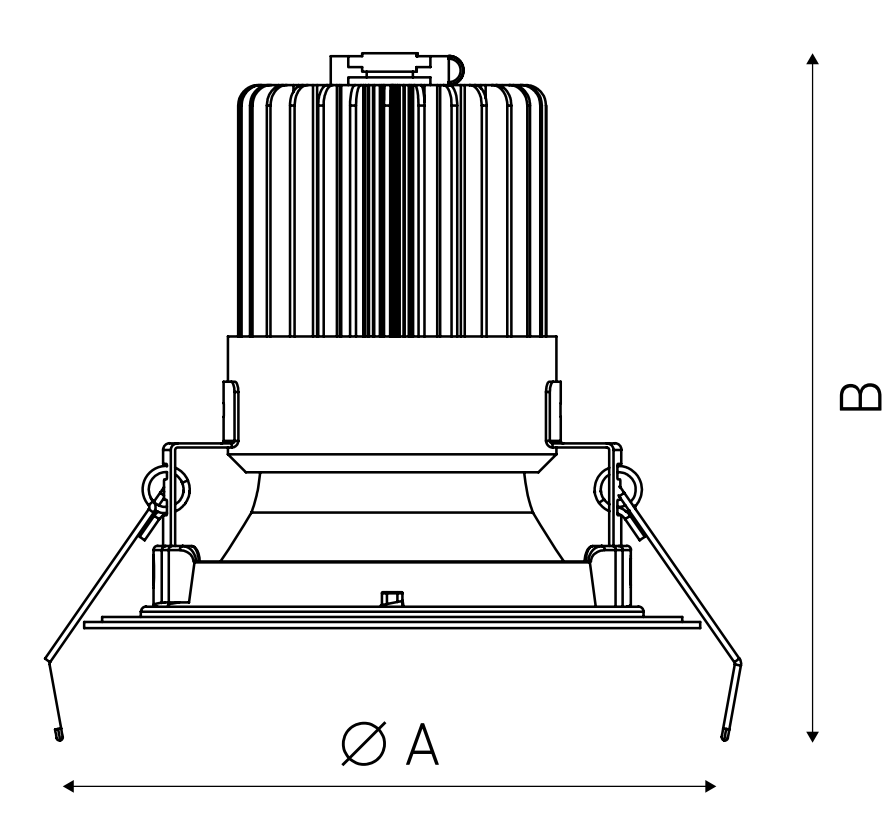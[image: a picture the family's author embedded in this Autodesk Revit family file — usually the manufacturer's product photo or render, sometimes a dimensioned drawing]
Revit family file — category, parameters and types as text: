
# Revit family: OKKO S
name_source: partatom
category: Осветительные приборы
revit_build: Autodesk Revit 2016 (Build: 20150220_1215(x64)
units: mm (PartAtom-declared; Revit-internal decimal feet)

## family parameters
Источник света = Да
Общий = Нет
Основа = Грань
При загрузке вырезать с полостями = Нет
Размер круглого соединителя = Использовать диаметр
Тип детали = Нормальный
Точка расчета площади = Нет

## types (1)
- OKKO S
    ADSK_Единица измерения = Шт.
    ADSK_Завод-изготовитель = ООО МГК Световые технологии
    ADSK_Количество фаз = 1
    ADSK_Количество фаз числовое = 1
    ADSK_Коэффициент мощности = 0.92
    ADSK_Масса = 0
    ADSK_Наименование = Накладной потолочный светодиодный светильник направленного света. Корпус светильника выполнен из алюминия, окрашенного матовой краской. Глубокая декоративная рамка из зеркального алюминия создает большой защитный угол и эффект выключенного источника света – dark light. Оптическая часть закрыта фасетчатым стеклом. Стандартный цвет WH – белый
    ADSK_Напряжение = 220 В
    ADSK_Номинальная мощность = 0 кВт
    ADSK_Полная мощность = 0 кВ·А
    ADSK_Размер_Высота = 100 мм
    ADSK_Размер_Диаметр = 120 мм
    ADSK_Ток = 0 А
    ADSK_Энергоэффективность = 0 лм/Вт
    IP Class = IP20
    URL = http://www.ltcompany.com
    Блок аварийного питания = Нет
    Видимая форма излучения при визуализации = Нет
    Группа модели = Светильники
    Изготовитель = ООО МГК Световые технологии
    Излучение по длине прямоугольника = 120 мм
    Излучение по ширине прямоугольника = 120 мм
    Класс Защиты = I
    Климатическая зона = УХЛ4
    Код по классификатору = D5020200
    Корпус = Белый пластик
    Область использования = HoReCa/гостиницы/рестораны/кафе, Конференц залы, Культурно-развлекательные учреждения, Магазины/бутики, Офисно-административные объекты, ТРЦ, Частные интерьеры
    Описание = Накладной потолочный светодиодный светильник направленного света. Корпус светильника выполнен из алюминия, окрашенного матовой краской. Глубокая декоративная рамка из зеркального алюминия создает большой защитный угол и эффект выключенного источника света – dark light. Оптическая часть закрыта фасетчатым стеклом. Стандартный цвет WH – белый
    Отметка по умолчанию = 60 мм
    Плафон = Плафон самосвечение
    Полная установленная мощность = 0 кВ·А
    Радиус = 60 мм
    Радиус.рефлектор = 50 мм
    Разработчик = ООО ПРОРУБИМ
    Разработчик (телефон) = +7 (495) 649-85-43
    Светофильтр = 16777215
    Смещение цветовой температуры при затухании лампы = <Нет>
    Тип ИС = LED
    Тип продукции = Cветильник
    Угол наклона = -90.00°
    Файл фотометрической сетки = generic
